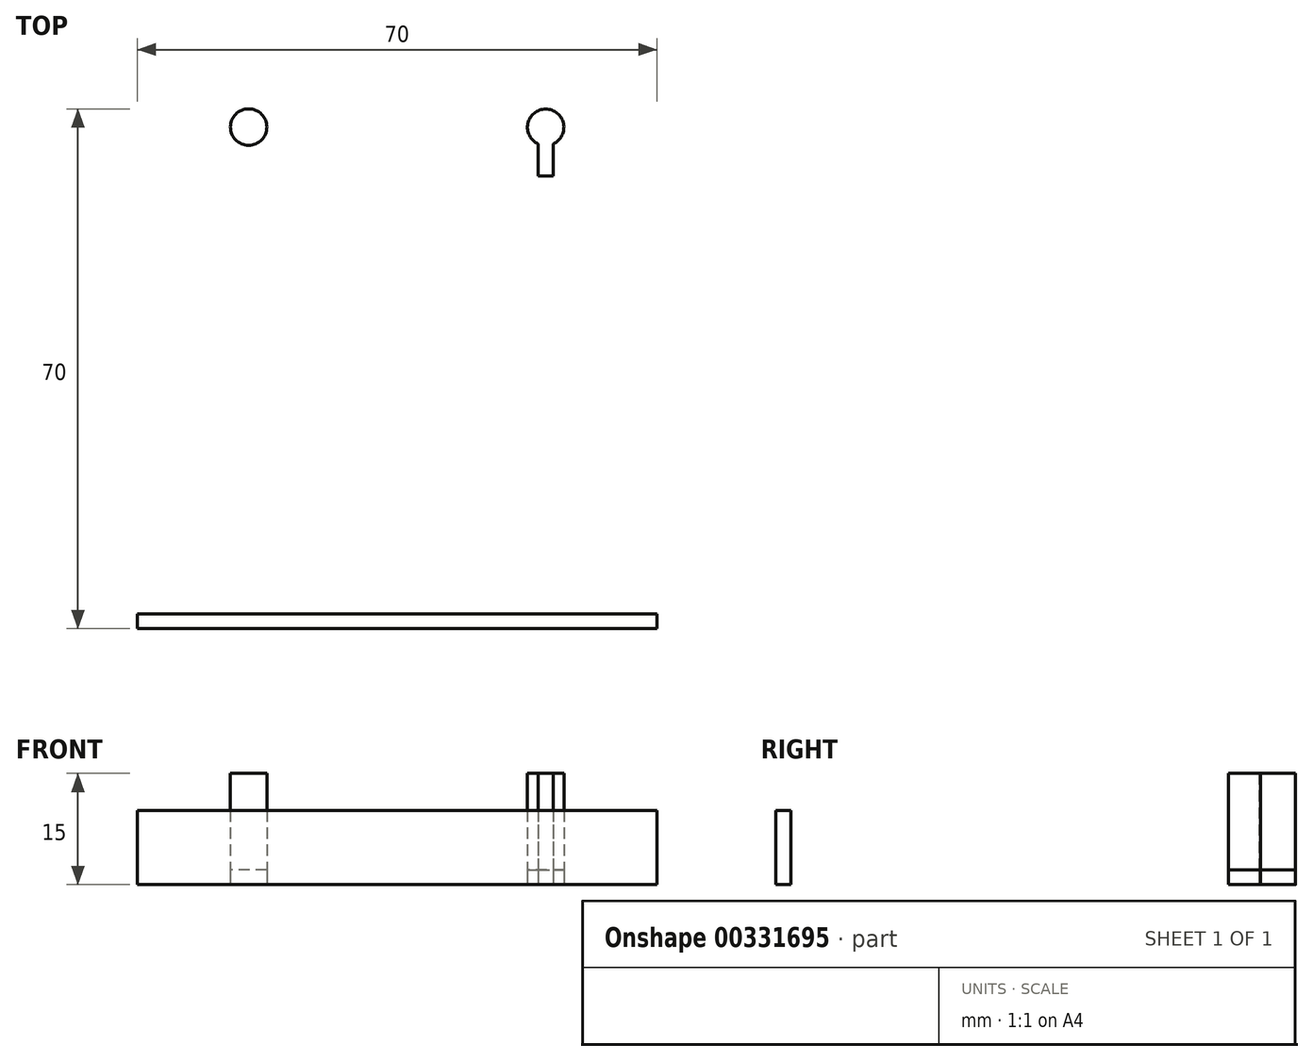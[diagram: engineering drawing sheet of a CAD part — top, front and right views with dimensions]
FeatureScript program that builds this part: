
annotation { "Feature Type Name" : "Feature", "Feature Type Description" : "" }
export const myFeature = defineFeature(function(context is Context, id is Id, definition is map)
    precondition{}
    {
        {
            var Q0;
            Q0=qCreatedBy(makeId("Top.planeOp"),FACE);
            var sketch = newSketch(context, id + "F0", { "sketchPlane" : qUnion([Q0])});
            skLineSegment(sketch, "E0.bottom", {"start": v(-35, 35) * mm, "end": v(35, 35) * mm});
            skLineSegment(sketch, "E0.top", {"start": v(-35, -35) * mm, "end": v(35, -35) * mm});
            skLineSegment(sketch, "E0.left", {"start": v(-35, 35) * mm, "end": v(-35, -35) * mm});
            skLineSegment(sketch, "E0.right", {"start": v(35, 35) * mm, "end": v(35, -35) * mm});
            skPoint(sketch, "E0.middle", {"position": v(0, 0) * mm});
            skLineSegment(sketch, "E1.top", {"start": v(21, 78.11) * mm, "end": v(21, 78.11) * mm});
            skLineSegment(sketch, "E2.top", {"start": v(-21, 78.11) * mm, "end": v(-21, 78.11) * mm});
            skCircle(sketch, "E3", {"center": v(-20, 32.55) * mm, "radius": 2.45 * mm});
            skCircle(sketch, "E4", {"center": v(20, 32.53) * mm, "radius": 2.45 * mm});
            skLineSegment(sketch, "E5", {"start": v(-21, 25.97) * mm, "end": v(-21, 30.31) * mm});
            skLineSegment(sketch, "E6", {"start": v(-21, 30.31) * mm, "end": v(-21, 25.97) * mm});
            skLineSegment(sketch, "E7", {"start": v(-19, 25.97) * mm, "end": v(-19, 30.31) * mm});
            skLineSegment(sketch, "E8", {"start": v(-19, 25.97) * mm, "end": v(-21, 25.97) * mm});
            skLineSegment(sketch, "E9", {"start": v(19, 25.97) * mm, "end": v(19, 30.31) * mm});
            skLineSegment(sketch, "E10", {"start": v(19, 25.97) * mm, "end": v(21, 25.97) * mm});
            skLineSegment(sketch, "E11", {"start": v(21, 25.97) * mm, "end": v(21, 30.31) * mm});
            skLineSegment(sketch, "E12", {"start": v(-35, -33) * mm, "end": v(35, -33) * mm});
            skSolve(sketch);
        }
        {
            var Q0;
            {var subQ0=sQuery(id+"F0.wireOp",EDGE,"E3");var subQ1=makeQuery(id+"F0.imprint","INTERSECT",VERTEX,{"derivedFrom":[subQ0,sQuery(id+"F0.wireOp",EDGE,"E6")]});Q0=makeQuery(id+"F0.imprint","IMPRINT",FACE,{"disambiguationData":[TD([[makeQuery(id+"F0.imprint","IMPRINT",EDGE,{"disambiguationData":[TD([[subQ1,1.0]])],"derivedFrom":subQ0}),1.0]])]});}
            var Q1;
            {var subQ0=sQuery(id+"F0.wireOp",EDGE,"E6");Q1=makeQuery(id+"F0.imprint","IMPRINT",FACE,{"disambiguationData":[TD([[makeQuery(id+"F0.imprint","IMPRINT",EDGE,{"derivedFrom":subQ0}),1.0]])]});}
            var Q2;
            {var subQ0=sQuery(id+"F0.wireOp",EDGE,"E4");var subQ1=makeQuery(id+"F0.imprint","INTERSECT",VERTEX,{"derivedFrom":[subQ0,sQuery(id+"F0.wireOp",EDGE,"E9")]});Q2=makeQuery(id+"F0.imprint","IMPRINT",FACE,{"disambiguationData":[TD([[makeQuery(id+"F0.imprint","IMPRINT",EDGE,{"disambiguationData":[TD([[subQ1,-1.0]])],"derivedFrom":subQ0}),1.0]])]});}
            var Q3;
            {var subQ5=sQuery(id+"F0.wireOp",EDGE,"E10");Q3=makeQuery(id+"F0.imprint","IMPRINT",FACE,{"disambiguationData":[TD([[makeQuery(id+"F0.imprint","IMPRINT",EDGE,{"derivedFrom":subQ5}),1.0]])]});}
            extrude(context, id + "F1", {"entities" : qUnion([Q0, Q1, Q2, Q3]), "depth" : 15 * mm});
        }
        {
            var Q0;
            {var subQ4=sQuery(id+"F0.wireOp",EDGE,"E6");Q0=makeQuery(id+"F0.imprint","IMPRINT",FACE,{"disambiguationData":[TD([[makeQuery(id+"F0.imprint","IMPRINT",EDGE,{"derivedFrom":subQ4}),-1.0]])]});}
            var Q1;
            {var subQ0=sQuery(id+"F0.wireOp",EDGE,"E6");Q1=makeQuery(id+"F0.imprint","IMPRINT",FACE,{"disambiguationData":[TD([[makeQuery(id+"F0.imprint","IMPRINT",EDGE,{"derivedFrom":subQ0}),1.0]])]});}
            var Q2;
            {var subQ0=sQuery(id+"F0.wireOp",EDGE,"E3");var subQ1=makeQuery(id+"F0.imprint","INTERSECT",VERTEX,{"derivedFrom":[subQ0,sQuery(id+"F0.wireOp",EDGE,"E6")]});Q2=makeQuery(id+"F0.imprint","IMPRINT",FACE,{"disambiguationData":[TD([[makeQuery(id+"F0.imprint","IMPRINT",EDGE,{"disambiguationData":[TD([[subQ1,1.0]])],"derivedFrom":subQ0}),1.0]])]});}
            var Q3;
            {var subQ0=sQuery(id+"F0.wireOp",EDGE,"E4");var subQ1=makeQuery(id+"F0.imprint","INTERSECT",VERTEX,{"derivedFrom":[subQ0,sQuery(id+"F0.wireOp",EDGE,"E9")]});Q3=makeQuery(id+"F0.imprint","IMPRINT",FACE,{"disambiguationData":[TD([[makeQuery(id+"F0.imprint","IMPRINT",EDGE,{"disambiguationData":[TD([[subQ1,-1.0]])],"derivedFrom":subQ0}),1.0]])]});}
            var Q4;
            {var subQ5=sQuery(id+"F0.wireOp",EDGE,"E10");Q4=makeQuery(id+"F0.imprint","IMPRINT",FACE,{"disambiguationData":[TD([[makeQuery(id+"F0.imprint","IMPRINT",EDGE,{"derivedFrom":subQ5}),1.0]])]});}
            var Q5;
            {var subQ0=sQuery(id+"F0.wireOp",EDGE,"E0.top");Q5=makeQuery(id+"F0.imprint","IMPRINT",FACE,{"disambiguationData":[TD([[makeQuery(id+"F0.imprint","IMPRINT",EDGE,{"derivedFrom":subQ0}),1.0]])]});}
            extrude(context, id + "F2", {"entities" : qUnion([Q0, Q1, Q2, Q3, Q4, Q5]), "depth" : 2 * mm});
        }
        {
            var Q0;
            {var subQ0=sQuery(id+"F0.wireOp",EDGE,"E0.top");Q0=makeQuery(id+"F0.imprint","IMPRINT",FACE,{"disambiguationData":[TD([[makeQuery(id+"F0.imprint","IMPRINT",EDGE,{"derivedFrom":subQ0}),1.0]])]});}
            extrude(context, id + "F3", {"entities" : qUnion([Q0]), "operationType" : NewBodyOperationType.ADD, "depth" : 10 * mm});
        }
    });
